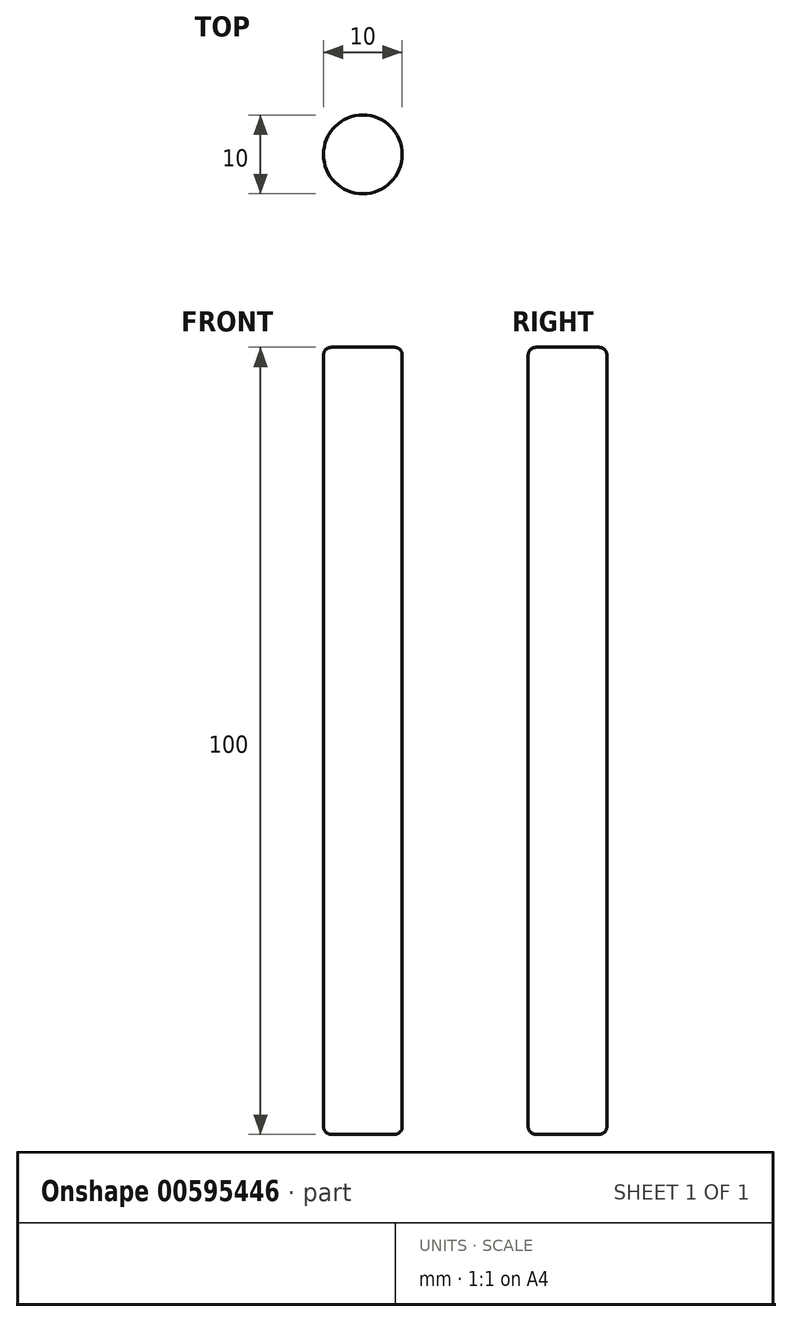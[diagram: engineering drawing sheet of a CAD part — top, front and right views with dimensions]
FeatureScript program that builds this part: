
annotation { "Feature Type Name" : "Feature", "Feature Type Description" : "" }
export const myFeature = defineFeature(function(context is Context, id is Id, definition is map)
    precondition{}
    {
        {
            var Q0;
            Q0=qCreatedBy(makeId("Top.planeOp"),FACE);
            var sketch = newSketch(context, id + "F0", { "sketchPlane" : qUnion([Q0])});
            skCircle(sketch, "E0", {"center": v(0, 0) * mm, "radius": 5 * mm});
            skSolve(sketch);
        }
        {
            var Q0;
            Q0 = qSketchRegion(id + "F0", true);
            extrude(context, id + "F1", {"entities" : qUnion([Q0]), "endBound" : BoundingType.SYMMETRIC, "depth" : 100 * mm, "offsetDistance" : 25 * mm});
        }
        {
            var Q0;
            Q0=makeQuery(id+"F1.opExtrude","CAP_EDGE",EDGE,{"disambiguationData":[OSD([sQuery(id+"F0.wireOp",EDGE,"E0")])],"isStart":false});
            fillet(context, id + "F2", {"entities" : qUnion([Q0]), "radius" : 1 * mm, "tangentPropagation" : true, "allowEdgeOverflow" : false});
        }
        {
            var Q0;
            Q0=makeQuery(id+"F1.opExtrude","CAP_EDGE",EDGE,{"disambiguationData":[OSD([sQuery(id+"F0.wireOp",EDGE,"E0")])],"isStart":true});
            fillet(context, id + "F3", {"entities" : qUnion([Q0]), "radius" : 1 * mm, "tangentPropagation" : true, "allowEdgeOverflow" : false});
        }
    });
